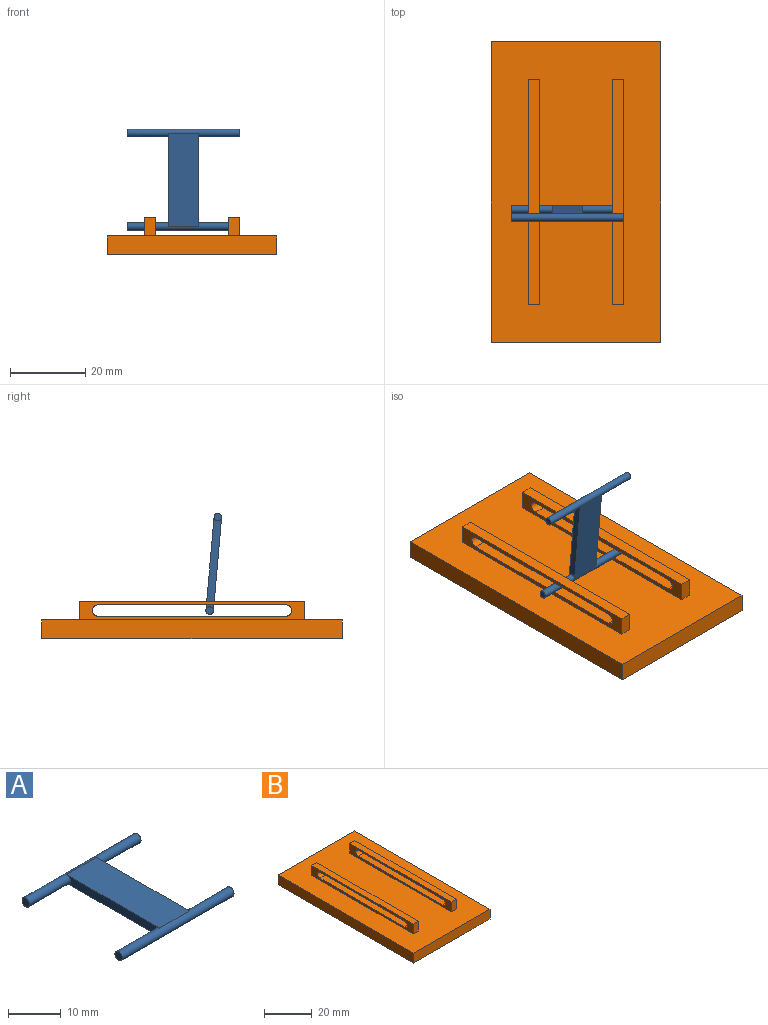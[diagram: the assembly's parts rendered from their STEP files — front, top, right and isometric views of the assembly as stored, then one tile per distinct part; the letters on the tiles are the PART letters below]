
ASSEMBLY  parts=2 mates=1
PART A: 10 faces, bbox 30x27x2 mm
  f0: plane 25x2mm, normal (-1,0,0), area 46.9mm2, adj f2,f3,f4,f6
  f1: plane 25x2mm, normal (1,0,0), area 46.9mm2, adj f2,f3,f4,f6
  f2: plane 25x8mm, normal (0,0,1), area 200mm2, adj f0,f1,f4,f6
  f3: plane 25x8mm, normal (0,0,-1), area 200mm2, adj f0,f1,f4,f6
  f4: cylinder r=1mm len=30mm, axis (-1,0,0), area 163.4mm2, adj f0,f1,f2,f3,f5,f8
  f5: plane 2x2mm, normal (1,0,0), area 3.1mm2, adj f4
  f6: cylinder r=1mm len=30mm, axis (-1,0,0), area 163.4mm2, adj f0,f1,f2,f3,f7,f9
  f7: plane 2x2mm, normal (1,0,0), area 3.1mm2, adj f6
  f8: plane 2x2mm, normal (-1,0,0), area 3.1mm2, adj f4
  f9: plane 2x2mm, normal (-1,0,0), area 3.1mm2, adj f6
PART B: 24 faces, bbox 45x80x10 mm
  f0: plane 80x45mm, normal (0,0,1), area 3240mm2, adj f1,f2,f3,f4,f6,f7,f8,f9
  f1: plane 45x5mm, normal (0,-1,0), area 225mm2, adj f0,f2,f4,f5
  f2: plane 80x5mm, normal (1,0,0), area 400mm2, adj f0,f1,f3,f5
  f3: plane 45x5mm, normal (0,1,0), area 225mm2, adj f0,f2,f4,f5
  f4: plane 80x5mm, normal (-1,0,0), area 400mm2, adj f0,f1,f3,f5
  f5: plane 80x45mm, normal (0,0,-1), area 3600mm2, adj f1,f2,f3,f4
  f6: plane 5x3mm, normal (0,-1,0), area 15mm2, adj f0,f7,f9,f10
  f7: plane 60x5mm, normal (1,0,0), area 142.9mm2, adj f0,f6,f8,f10,f20,f21,f22,f23
  f8: plane 5x3mm, normal (0,1,0), area 15mm2, adj f0,f7,f9,f10
  f9: plane 60x5mm, normal (-1,0,0), area 142.9mm2, adj f0,f6,f8,f10,f20,f21,f22,f23
  f10: plane 60x3mm, normal (0,0,1), area 180mm2, adj f6,f7,f8,f9
  f11: plane 60x5mm, normal (1,0,0), area 142.9mm2, adj f0,f12,f14,f15,f16,f17,f18,f19
  f12: plane 5x3mm, normal (0,1,0), area 15mm2, adj f0,f11,f13,f15
  f13: plane 60x5mm, normal (-1,0,0), area 142.9mm2, adj f0,f12,f14,f15,f16,f17,f18,f19
  f14: plane 5x3mm, normal (0,-1,0), area 15mm2, adj f0,f11,f13,f15
  f15: plane 60x3mm, normal (0,0,1), area 180mm2, adj f11,f12,f13,f14
  f16: plane 50x3mm, normal (0,0,-1), area 150mm2, adj f11,f13,f17,f19
  f17: cylinder r=1.5mm len=3mm, axis (-1,0,0), area 14.1mm2, adj f11,f13,f16,f18
  f18: plane 50x3mm, normal (0,0,1), area 150mm2, adj f11,f13,f17,f19
  f19: cylinder r=1.5mm len=3mm, axis (-1,0,0), area 14.1mm2, adj f11,f13,f16,f18
  f20: cylinder r=1.5mm len=3mm, axis (-1,0,0), area 14.1mm2, adj f7,f9,f21,f23
  f21: plane 50x3mm, normal (0,0,1), area 150mm2, adj f7,f9,f20,f22
  f22: cylinder r=1.5mm len=3mm, axis (-1,0,0), area 14.1mm2, adj f7,f9,f21,f23
  f23: plane 50x3mm, normal (0,0,-1), area 150mm2, adj f7,f9,f20,f22
PLACE A rot(axis=(-1,0,0),85deg) t=(-64.3,-23.63,67.42)mm
PLACE B t=(-22.32,-13.89,13.85)mm fixed
MATE pin_slot A.f6 <-> B.f17  axis (1,0,0) through (-9.57,-18.59,21.35)mm
